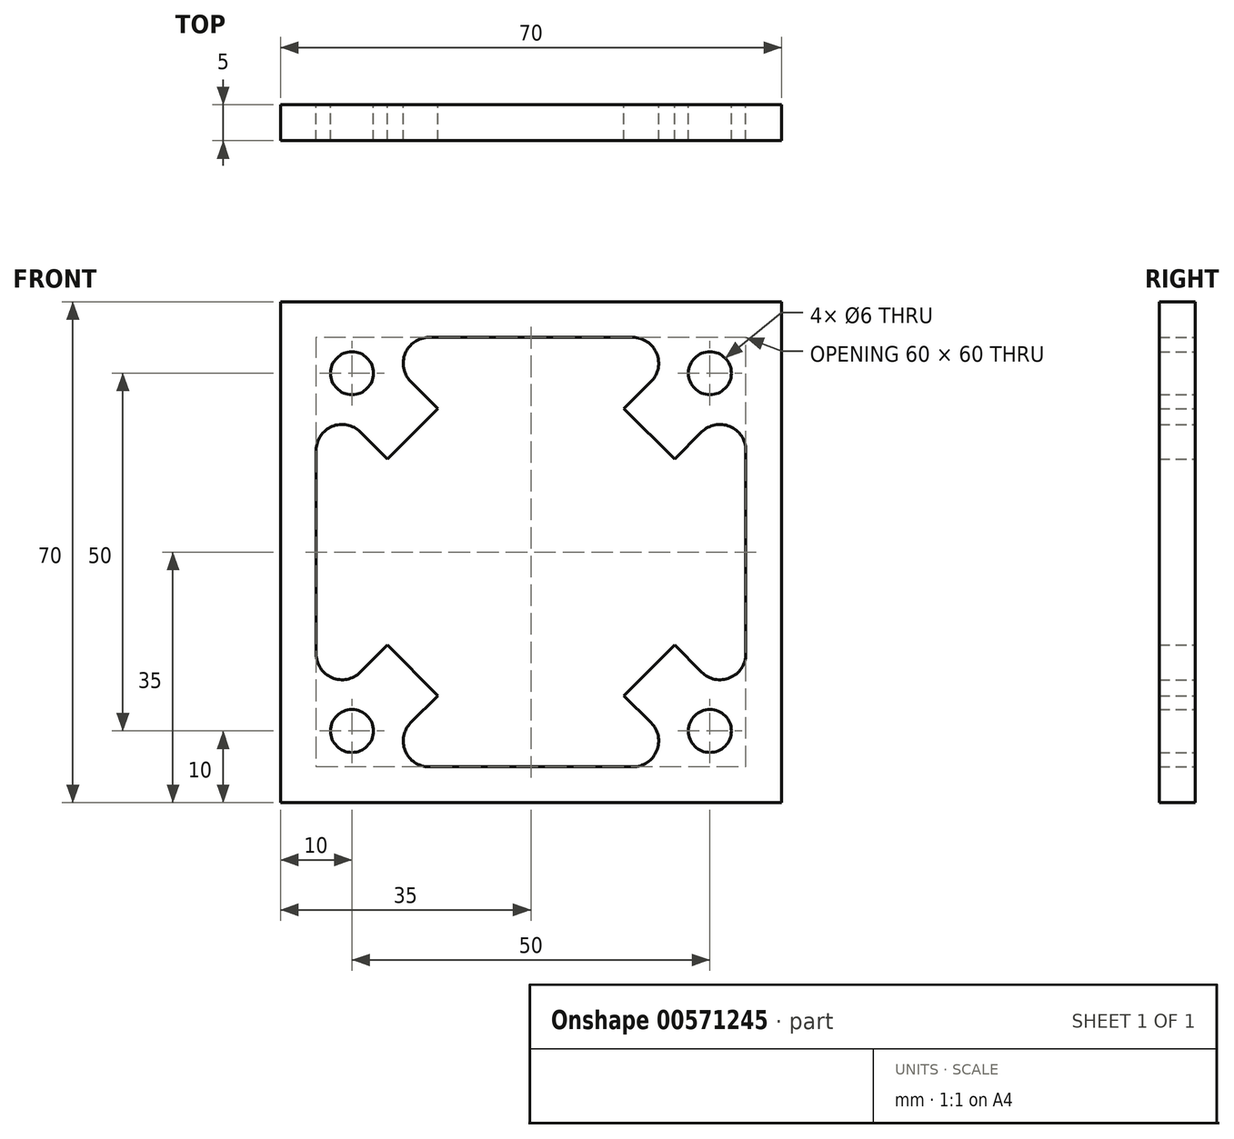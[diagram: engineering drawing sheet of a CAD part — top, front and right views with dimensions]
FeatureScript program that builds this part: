
annotation { "Feature Type Name" : "Feature", "Feature Type Description" : "" }
export const myFeature = defineFeature(function(context is Context, id is Id, definition is map)
    precondition{}
    {
        {
            var Q0;
            Q0=qCreatedBy(makeId("Front.planeOp"),FACE);
            var sketch = newSketch(context, id + "F0", { "sketchPlane" : qUnion([Q0])});
            skLineSegment(sketch, "E0", {"start": v(0, 0) * mm, "end": v(0, 35) * mm});
            skLineSegment(sketch, "E1", {"start": v(0, 35) * mm, "end": v(35, 35) * mm});
            skLineSegment(sketch, "E2", {"start": v(0, 0) * mm, "end": v(5, 0) * mm});
            skLineSegment(sketch, "E3", {"start": v(5, 0) * mm, "end": v(5, 14.24) * mm});
            skLineSegment(sketch, "E4", {"start": v(35, 35) * mm, "end": v(35, 30) * mm});
            skLineSegment(sketch, "E5", {"start": v(35, 30) * mm, "end": v(20.76, 30) * mm});
            skCircle(sketch, "E6", {"center": v(10, 25) * mm, "radius": 3 * mm});
            skLineSegment(sketch, "E7", {"start": v(14.93, 13) * mm, "end": v(22, 20.07) * mm});
            skLineSegment(sketch, "E8", {"start": v(14.93, 13) * mm, "end": v(11.15, 16.78) * mm});
            skLineSegment(sketch, "E9", {"start": v(22, 20.07) * mm, "end": v(18.22, 23.85) * mm});
            skArc(sketch, "E10.filletArc", {"start": v(11.15, 16.78) * mm, "mid": v(7.22, 17.56) * mm, "end": v(5, 14.24) * mm});
            skArc(sketch, "E11.filletArc", {"start": v(20.76, 30) * mm, "mid": v(17.44, 27.78) * mm, "end": v(18.22, 23.85) * mm});
            skLineSegment(sketch, "E12", {"start": v(14.93, 13) * mm, "end": v(5, 13) * mm, "construction": true});
            skLineSegment(sketch, "E13.1.0", {"start": v(22, -20.07) * mm, "end": v(14.93, -13) * mm});
            skArc(sketch, "E13.1.1", {"start": v(18.22, -23.85) * mm, "mid": v(17.44, -27.78) * mm, "end": v(20.76, -30) * mm});
            skLineSegment(sketch, "E13.1.2", {"start": v(22, -20.07) * mm, "end": v(18.22, -23.85) * mm});
            skLineSegment(sketch, "E13.1.3", {"start": v(14.93, -13) * mm, "end": v(11.15, -16.78) * mm});
            skLineSegment(sketch, "E13.1.4", {"start": v(35, -35) * mm, "end": v(35, -30) * mm});
            skCircle(sketch, "E13.1.6", {"center": v(10, -25) * mm, "radius": 3 * mm});
            skLineSegment(sketch, "E13.1.7", {"start": v(5, 0) * mm, "end": v(5, -14.24) * mm});
            skArc(sketch, "E13.1.8", {"start": v(5, -14.24) * mm, "mid": v(7.22, -17.56) * mm, "end": v(11.15, -16.78) * mm});
            skLineSegment(sketch, "E13.1.9", {"start": v(22, -20.07) * mm, "end": v(22, -30) * mm, "construction": true});
            skLineSegment(sketch, "E13.1.10", {"start": v(35, -30) * mm, "end": v(20.76, -30) * mm});
            skLineSegment(sketch, "E13.1.11", {"start": v(0, -35) * mm, "end": v(0, 0) * mm});
            skLineSegment(sketch, "E13.1.12", {"start": v(35, -35) * mm, "end": v(0, -35) * mm});
            skLineSegment(sketch, "E13.2.0", {"start": v(55.07, -13) * mm, "end": v(48, -20.07) * mm});
            skArc(sketch, "E13.2.1", {"start": v(58.85, -16.78) * mm, "mid": v(62.78, -17.56) * mm, "end": v(65, -14.24) * mm});
            skLineSegment(sketch, "E13.2.2", {"start": v(55.07, -13) * mm, "end": v(58.85, -16.78) * mm});
            skLineSegment(sketch, "E13.2.3", {"start": v(48, -20.07) * mm, "end": v(51.78, -23.85) * mm});
            skLineSegment(sketch, "E13.2.4", {"start": v(70, 0) * mm, "end": v(65, 0) * mm});
            skLineSegment(sketch, "E13.2.5", {"start": v(35, -35) * mm, "end": v(35, -30) * mm});
            skCircle(sketch, "E13.2.6", {"center": v(60, -25) * mm, "radius": 3 * mm});
            skLineSegment(sketch, "E13.2.7", {"start": v(35, -30) * mm, "end": v(49.24, -30) * mm});
            skArc(sketch, "E13.2.8", {"start": v(49.24, -30) * mm, "mid": v(52.56, -27.78) * mm, "end": v(51.78, -23.85) * mm});
            skLineSegment(sketch, "E13.2.9", {"start": v(55.07, -13) * mm, "end": v(65, -13) * mm, "construction": true});
            skLineSegment(sketch, "E13.2.10", {"start": v(65, 0) * mm, "end": v(65, -14.24) * mm});
            skLineSegment(sketch, "E13.2.11", {"start": v(70, -35) * mm, "end": v(35, -35) * mm});
            skLineSegment(sketch, "E13.2.12", {"start": v(70, 0) * mm, "end": v(70, -35) * mm});
            skLineSegment(sketch, "E13.3.0", {"start": v(48, 20.07) * mm, "end": v(55.07, 13) * mm});
            skArc(sketch, "E13.3.1", {"start": v(51.78, 23.85) * mm, "mid": v(52.56, 27.78) * mm, "end": v(49.24, 30) * mm});
            skLineSegment(sketch, "E13.3.2", {"start": v(48, 20.07) * mm, "end": v(51.78, 23.85) * mm});
            skLineSegment(sketch, "E13.3.3", {"start": v(55.07, 13) * mm, "end": v(58.85, 16.78) * mm});
            skLineSegment(sketch, "E13.3.5", {"start": v(70, 0) * mm, "end": v(65, 0) * mm});
            skCircle(sketch, "E13.3.6", {"center": v(60, 25) * mm, "radius": 3 * mm});
            skLineSegment(sketch, "E13.3.7", {"start": v(65, 0) * mm, "end": v(65, 14.24) * mm});
            skArc(sketch, "E13.3.8", {"start": v(65, 14.24) * mm, "mid": v(62.78, 17.56) * mm, "end": v(58.85, 16.78) * mm});
            skLineSegment(sketch, "E13.3.9", {"start": v(48, 20.07) * mm, "end": v(48, 30) * mm, "construction": true});
            skLineSegment(sketch, "E13.3.10", {"start": v(35, 30) * mm, "end": v(49.24, 30) * mm});
            skLineSegment(sketch, "E13.3.11", {"start": v(70, 35) * mm, "end": v(70, 0) * mm});
            skLineSegment(sketch, "E13.3.12", {"start": v(35, 35) * mm, "end": v(70, 35) * mm});
            skPoint(sketch, "E13.center", {"position": v(35, 0) * mm});
            skSolve(sketch);
        }
        {
            var Q0;
            Q0=makeQuery(id+"F0.imprint","IMPRINT",FACE,{"disambiguationData":[TD([[makeQuery(id+"F0.imprint","IMPRINT",EDGE,{"derivedFrom":sQuery(id+"F0.wireOp",EDGE,"E0")}),-1.0]])]});
            var Q1;
            Q1=makeQuery(id+"F0.imprint","IMPRINT",FACE,{"disambiguationData":[TD([[makeQuery(id+"F0.imprint","IMPRINT",EDGE,{"derivedFrom":sQuery(id+"F0.wireOp",EDGE,"E13.3.0")}),1.0]])]});
            var Q2;
            Q2=makeQuery(id+"F0.imprint","IMPRINT",FACE,{"disambiguationData":[TD([[makeQuery(id+"F0.imprint","IMPRINT",EDGE,{"derivedFrom":sQuery(id+"F0.wireOp",EDGE,"E13.2.0")}),1.0]])]});
            var Q3;
            Q3=makeQuery(id+"F0.imprint","IMPRINT",FACE,{"disambiguationData":[TD([[makeQuery(id+"F0.imprint","IMPRINT",EDGE,{"derivedFrom":sQuery(id+"F0.wireOp",EDGE,"E13.1.0")}),1.0]])]});
            extrude(context, id + "F1", {"entities" : qUnion([Q0, Q1, Q2, Q3]), "depth" : 5 * mm, "offsetDistance" : 25 * mm});
        }
    });
